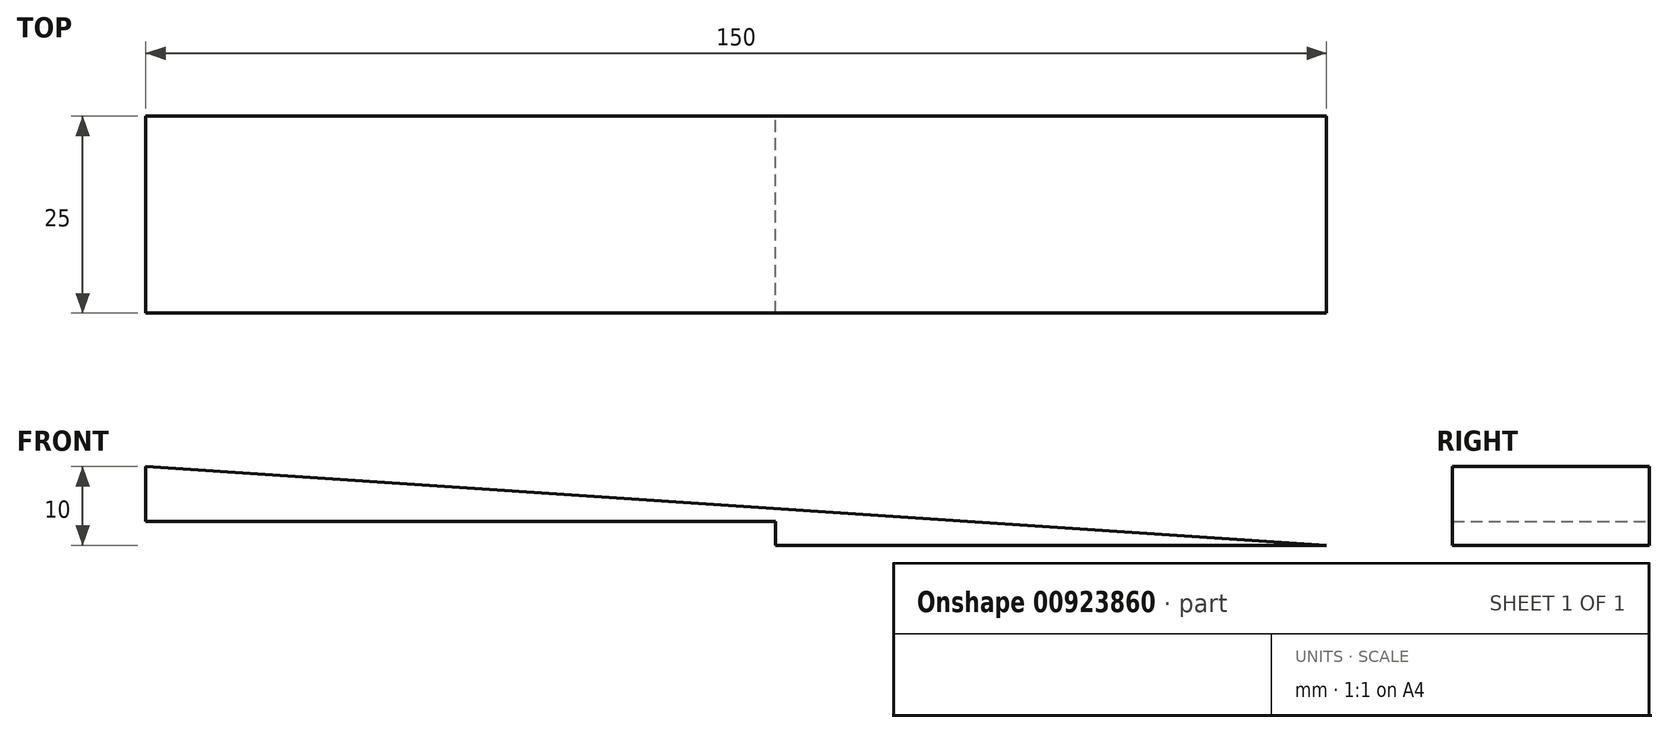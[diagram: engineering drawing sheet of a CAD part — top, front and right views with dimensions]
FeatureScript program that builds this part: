
annotation { "Feature Type Name" : "Feature", "Feature Type Description" : "" }
export const myFeature = defineFeature(function(context is Context, id is Id, definition is map)
    precondition{}
    {
        {
            var Q0;
            Q0=qCreatedBy(makeId("Front.planeOp"),FACE);
            var sketch = newSketch(context, id + "F0", { "sketchPlane" : qUnion([Q0])});
            skLineSegment(sketch, "E0", {"start": v(0, 3) * mm, "end": v(0, 10) * mm});
            skLineSegment(sketch, "E1", {"start": v(0, 10) * mm, "end": v(150, 0) * mm});
            skLineSegment(sketch, "E2", {"start": v(150, 0) * mm, "end": v(80, 0) * mm});
            skLineSegment(sketch, "E3", {"start": v(80, 0) * mm, "end": v(80, 3) * mm});
            skLineSegment(sketch, "E4", {"start": v(80, 3) * mm, "end": v(0, 3) * mm});
            skSolve(sketch);
        }
        {
            var Q0;
            Q0=makeQuery(id+"F0.imprint","IMPRINT",FACE,{"disambiguationData":[TD([[makeQuery(id+"F0.imprint","IMPRINT",EDGE,{"derivedFrom":sQuery(id+"F0.wireOp",EDGE,"E0")}),-1.0]])]});
            extrude(context, id + "F1", {"entities" : qUnion([Q0]), "depth" : 25 * mm, "offsetDistance" : 25 * mm});
        }
    });
